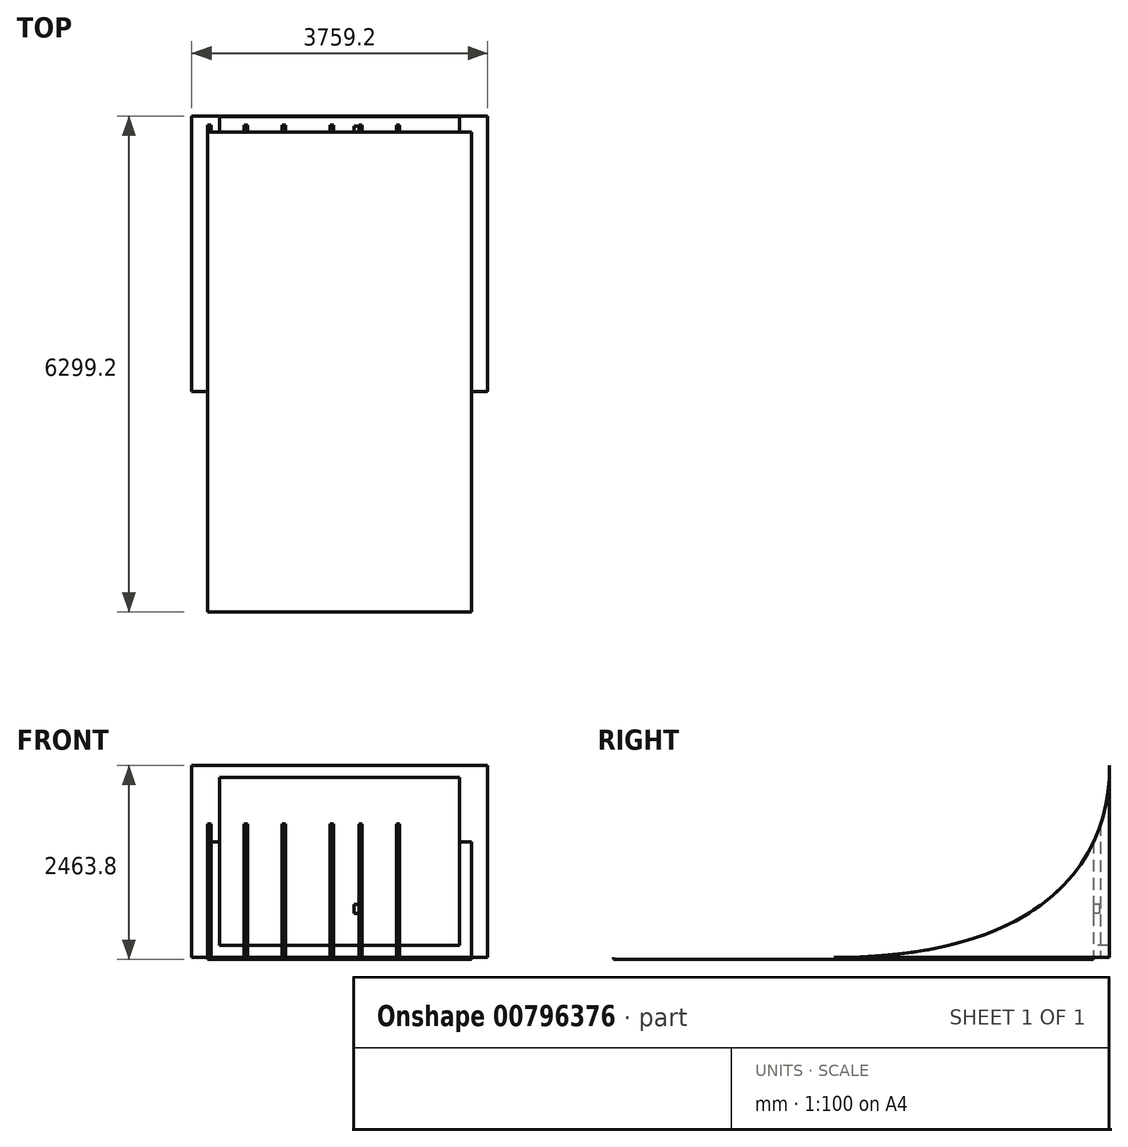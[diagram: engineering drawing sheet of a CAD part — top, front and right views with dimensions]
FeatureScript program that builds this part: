
annotation { "Feature Type Name" : "Feature", "Feature Type Description" : "" }
export const myFeature = defineFeature(function(context is Context, id is Id, definition is map)
    precondition{}
    {
        {
            var Q0;
            Q0=qCreatedBy(makeId("Top.planeOp"),FACE);
            var sketch = newSketch(context, id + "F0", { "sketchPlane" : qUnion([Q0])});
            skLineSegment(sketch, "E0.bottom", {"start": v(-1681.8, 4149.45) * mm, "end": v(1671, 4149.45) * mm});
            skLineSegment(sketch, "E0.top", {"start": v(-1681.8, -1946.55) * mm, "end": v(1671, -1946.55) * mm});
            skLineSegment(sketch, "E0.left", {"start": v(-1681.8, 4149.45) * mm, "end": v(-1681.8, -1946.55) * mm});
            skLineSegment(sketch, "E0.right", {"start": v(1671, 4149.45) * mm, "end": v(1671, -1946.55) * mm});
            skSolve(sketch);
        }
        {
            var Q0;
            Q0=makeQuery(id+"F0.imprint","IMPRINT",FACE,{"disambiguationData":[TD([[makeQuery(id+"F0.imprint","IMPRINT",EDGE,{"derivedFrom":sQuery(id+"F0.wireOp",EDGE,"E0.bottom")}),-1.0]])]});
            extrude(context, id + "F1", {"entities" : qUnion([Q0]), "depth" : 25.4 * mm, "offsetDistance" : 25.4 * mm});
        }
        {
            var Q0;
            Q0=makeQuery(id+"F1.opExtrude","CAP_FACE",FACE,{"disambiguationData":[OSD([sQuery(id+"F0.wireOp",EDGE,"E0.bottom"),sQuery(id+"F0.wireOp",EDGE,"E0.top"),sQuery(id+"F0.wireOp",EDGE,"E0.left"),sQuery(id+"F0.wireOp",EDGE,"E0.right")])],"isStart":false});
            var sketch = newSketch(context, id + "F2", { "sketchPlane" : qUnion([Q0])});
            skLineSegment(sketch, "E1.left", {"start": v(-1681.8, 4149.45) * mm, "end": v(-1681.8, -1946.55) * mm});
            skLineSegment(sketch, "E2.left", {"start": v(1671, 4149.45) * mm, "end": v(1671, -1946.55) * mm});
            skLineSegment(sketch, "E3.0", {"start": v(-1885, 4352.65) * mm, "end": v(-1885, -1946.55) * mm});
            skLineSegment(sketch, "E3.1", {"start": v(-1885, 4352.65) * mm, "end": v(1874.2, 4352.65) * mm});
            skLineSegment(sketch, "E3.2", {"start": v(1874.2, 4352.65) * mm, "end": v(1874.2, -1946.55) * mm});
            skLineSegment(sketch, "E4", {"start": v(-1885, -1946.55) * mm, "end": v(-1681.8, -1946.55) * mm});
            skLineSegment(sketch, "E5", {"start": v(1671, -1946.55) * mm, "end": v(1874.2, -1946.55) * mm});
            skSolve(sketch);
        }
        {
            var Q0;
            Q0=makeQuery(id+"F2.imprint","IMPRINT",FACE,{"disambiguationData":[TD([[makeQuery(id+"F2.imprint","IMPRINT",EDGE,{"derivedFrom":sQuery(id+"F2.wireOp",EDGE,"E1.left")}),-1.0]])]});
            extrude(context, id + "F3", {"entities" : qUnion([Q0]), "depth" : 2438.4 * mm, "offsetDistance" : 25.4 * mm});
        }
        {
            var Q0;
            Q0=makeQuery(id+"F3.opExtrude","SWEPT_FACE",FACE,{"disambiguationData":[OSD([sQuery(id+"F2.wireOp",EDGE,"E3.2")])]});
            var sketch = newSketch(context, id + "F4", { "sketchPlane" : qUnion([Q0])});
            skLineSegment(sketch, "E6", {"start": v(4352.65, 25.4) * mm, "end": v(852.14, 25.4) * mm, "construction": true});
            skFitSpline(sketch, "E7", {"points": [v(4352.65, 2463.8) * mm, v(852.14, 25.4) * mm], "startDerivative": vector(0, -3890.45) * mm, "endDerivative": vector(-7720.83, 0) * mm});
            skSolve(sketch);
        }
        {
            var Q0;
            Q0=makeQuery(id+"F3.opExtrude","SWEPT_FACE",FACE,{"disambiguationData":[OSD([sQuery(id+"F0.wireOp",EDGE,"E0.bottom")])]});
            var sketch = newSketch(context, id + "F5", { "sketchPlane" : qUnion([Q0])});
            skLineSegment(sketch, "E8.0", {"start": v(-1529.4, 2311.4) * mm, "end": v(-1529.4, 177.8) * mm});
            skLineSegment(sketch, "E8.1", {"start": v(-1529.4, 2311.4) * mm, "end": v(1518.6, 2311.4) * mm});
            skLineSegment(sketch, "E8.2", {"start": v(1518.6, 2311.4) * mm, "end": v(1518.6, 177.8) * mm});
            skLineSegment(sketch, "E8.3", {"start": v(-1529.4, 177.8) * mm, "end": v(1518.6, 177.8) * mm});
            skLineSegment(sketch, "E9.0", {"start": v(1664.65, 31.75) * mm, "end": v(1664.65, 2457.45) * mm});
            skLineSegment(sketch, "E9.1", {"start": v(-1675.45, 31.75) * mm, "end": v(1664.65, 31.75) * mm});
            skLineSegment(sketch, "E9.2", {"start": v(-1675.45, 2457.45) * mm, "end": v(-1675.45, 31.75) * mm});
            skLineSegment(sketch, "E9.3", {"start": v(1664.65, 2457.45) * mm, "end": v(-1675.45, 2457.45) * mm});
            skSolve(sketch);
        }
        {
            var Q0;
            Q0=makeQuery(id+"F5.imprint","IMPRINT",FACE,{"disambiguationData":[TD([[makeQuery(id+"F5.imprint","IMPRINT",EDGE,{"derivedFrom":sQuery(id+"F5.wireOp",EDGE,"E8.0")}),1.0]])]});
            extrude(context, id + "F6", {"entities" : qUnion([Q0]), "operationType" : NewBodyOperationType.REMOVE, "endBound" : BoundingType.UP_TO_NEXT, "oppositeDirection" : true, "depth" : 203.2 * mm, "offsetDistance" : 25.4 * mm});
        }
        {
            var Q0;
            Q0=makeQuery(id+"F3.opExtrude","SWEPT_FACE",FACE,{"disambiguationData":[OSD([sQuery(id+"F0.wireOp",EDGE,"E0.bottom")])]});
            var sketch = newSketch(context, id + "F7", { "sketchPlane" : qUnion([Q0])});
            skLineSegment(sketch, "E10.bottom", {"start": v(-1681.8, 2463.8) * mm, "end": v(-1638.62, 2463.8) * mm});
            skLineSegment(sketch, "E10.top", {"start": v(-1681.8, 25.4) * mm, "end": v(-1638.62, 25.4) * mm});
            skLineSegment(sketch, "E10.left", {"start": v(-1681.8, 2463.8) * mm, "end": v(-1681.8, 25.4) * mm});
            skLineSegment(sketch, "E10.right", {"start": v(-1638.62, 2463.8) * mm, "end": v(-1638.62, 25.4) * mm});
            skLineSegment(sketch, "E11.bottom", {"start": v(-1220.8, 2463.8) * mm, "end": v(-1177.61, 2463.8) * mm});
            skLineSegment(sketch, "E11.top", {"start": v(-1220.8, 25.4) * mm, "end": v(-1177.61, 25.4) * mm});
            skLineSegment(sketch, "E11.left", {"start": v(-1220.8, 2463.8) * mm, "end": v(-1220.8, 25.4) * mm});
            skLineSegment(sketch, "E11.right", {"start": v(-1177.61, 2463.8) * mm, "end": v(-1177.61, 25.4) * mm});
            skLineSegment(sketch, "E12", {"start": v(-1199.2, 2463.8) * mm, "end": v(-1681.8, 2463.8) * mm});
            skLineSegment(sketch, "E13.bottom", {"start": v(-738.2, 2463.8) * mm, "end": v(-695.01, 2463.8) * mm});
            skLineSegment(sketch, "E13.top", {"start": v(-738.2, 25.4) * mm, "end": v(-695.01, 25.4) * mm});
            skLineSegment(sketch, "E13.left", {"start": v(-738.2, 2463.8) * mm, "end": v(-738.2, 25.4) * mm});
            skLineSegment(sketch, "E13.right", {"start": v(-695.01, 2463.8) * mm, "end": v(-695.01, 25.4) * mm});
            skLineSegment(sketch, "E14", {"start": v(-1681.8, 2463.8) * mm, "end": v(-716.6, 2463.8) * mm});
            skLineSegment(sketch, "E15.bottom", {"start": v(-128.6, 2463.8) * mm, "end": v(-85.41, 2463.8) * mm});
            skLineSegment(sketch, "E15.top", {"start": v(-128.6, 25.4) * mm, "end": v(-85.41, 25.4) * mm});
            skLineSegment(sketch, "E15.left", {"start": v(-128.6, 2463.8) * mm, "end": v(-128.6, 25.4) * mm});
            skLineSegment(sketch, "E15.right", {"start": v(-85.41, 2463.8) * mm, "end": v(-85.41, 25.4) * mm});
            skLineSegment(sketch, "E16", {"start": v(-107, 2463.8) * mm, "end": v(-1681.8, 2463.8) * mm});
            skLineSegment(sketch, "E17.bottom", {"start": v(237.17, 2463.8) * mm, "end": v(280.35, 2463.8) * mm});
            skLineSegment(sketch, "E17.top", {"start": v(237.17, 25.4) * mm, "end": v(280.35, 25.4) * mm});
            skLineSegment(sketch, "E17.left", {"start": v(237.17, 2463.8) * mm, "end": v(237.17, 25.4) * mm});
            skLineSegment(sketch, "E17.right", {"start": v(280.35, 2463.8) * mm, "end": v(280.35, 25.4) * mm});
            skLineSegment(sketch, "E18", {"start": v(258.76, 2463.8) * mm, "end": v(-1681.8, 2463.8) * mm});
            skLineSegment(sketch, "E19.bottom", {"start": v(712.65, 2463.8) * mm, "end": v(755.83, 2463.8) * mm});
            skLineSegment(sketch, "E19.top", {"start": v(712.65, 25.4) * mm, "end": v(755.83, 25.4) * mm});
            skLineSegment(sketch, "E19.left", {"start": v(712.65, 2463.8) * mm, "end": v(712.65, 25.4) * mm});
            skLineSegment(sketch, "E19.right", {"start": v(755.83, 2463.8) * mm, "end": v(755.83, 25.4) * mm});
            skLineSegment(sketch, "E20", {"start": v(734.24, 2463.8) * mm, "end": v(-1681.8, 2463.8) * mm});
            skSolve(sketch);
        }
        {
            var Q0;
            Q0 = qSketchRegion(id + "F7", true);
            extrude(context, id + "F8", {"entities" : qUnion([Q0]), "oppositeDirection" : true, "depth" : 88.9 * mm, "offsetDistance" : 25.4 * mm});
        }
        {
            var Q0;
            {var subQ0=sQuery(id+"F7.wireOp",EDGE,"E20");Q0=makeQuery(id+"F8.boolean.opBoolean","MERGE",FACE,{"derivedFrom":[makeQuery(id+"F3.opExtrude","SWEPT_FACE",FACE,{"disambiguationData":[OSD([sQuery(id+"F0.wireOp",EDGE,"E0.bottom")])]}),makeQuery(id+"F8.opExtrude","CAP_FACE",FACE,{"disambiguationData":[OSD([sQuery(id+"F7.wireOp",EDGE,"E11.top"),sQuery(id+"F7.wireOp",EDGE,"E11.left"),sQuery(id+"F7.wireOp",EDGE,"E11.right"),subQ0])],"isStart":true}),makeQuery(id+"F8.opExtrude","CAP_FACE",FACE,{"disambiguationData":[OSD([sQuery(id+"F7.wireOp",EDGE,"E13.top"),sQuery(id+"F7.wireOp",EDGE,"E13.left"),sQuery(id+"F7.wireOp",EDGE,"E13.right"),subQ0])],"isStart":true}),makeQuery(id+"F8.opExtrude","CAP_FACE",FACE,{"disambiguationData":[OSD([sQuery(id+"F7.wireOp",EDGE,"E15.top"),sQuery(id+"F7.wireOp",EDGE,"E15.left"),sQuery(id+"F7.wireOp",EDGE,"E15.right"),subQ0])],"isStart":true}),makeQuery(id+"F8.opExtrude","CAP_FACE",FACE,{"disambiguationData":[OSD([sQuery(id+"F7.wireOp",EDGE,"E17.top"),sQuery(id+"F7.wireOp",EDGE,"E17.left"),sQuery(id+"F7.wireOp",EDGE,"E17.right"),subQ0])],"isStart":true}),makeQuery(id+"F8.opExtrude","CAP_FACE",FACE,{"disambiguationData":[OSD([sQuery(id+"F7.wireOp",EDGE,"E19.bottom"),sQuery(id+"F7.wireOp",EDGE,"E19.top"),sQuery(id+"F7.wireOp",EDGE,"E19.left"),sQuery(id+"F7.wireOp",EDGE,"E19.right"),subQ0])],"isStart":true})]});}
            var sketch = newSketch(context, id + "F9", { "sketchPlane" : qUnion([Q0])});
            skLineSegment(sketch, "E21.bottom", {"start": v(237.17, 698.5) * mm, "end": v(173.67, 698.5) * mm});
            skLineSegment(sketch, "E21.top", {"start": v(237.17, 584.2) * mm, "end": v(173.67, 584.2) * mm});
            skLineSegment(sketch, "E21.left", {"start": v(237.17, 698.5) * mm, "end": v(237.17, 584.2) * mm});
            skLineSegment(sketch, "E21.right", {"start": v(173.67, 698.5) * mm, "end": v(173.67, 584.2) * mm});
            skLineSegment(sketch, "E22", {"start": v(237.17, 584.2) * mm, "end": v(237.17, 177.8) * mm, "construction": true});
            skCircle(sketch, "E23", {"center": v(206.47, 669.37) * mm, "radius": 18.27 * mm});
            skLineSegment(sketch, "E24", {"start": v(173.67, 641.35) * mm, "end": v(237.17, 641.35) * mm});
            skCircle(sketch, "E25", {"center": v(206.48, 613.44) * mm, "radius": 18.27 * mm});
            skLineSegment(sketch, "E26", {"start": v(200.19, 622.8) * mm, "end": v(200.19, 611.5) * mm});
            skLineSegment(sketch, "E27", {"start": v(213.83, 623.18) * mm, "end": v(213.83, 611.51) * mm});
            skLineSegment(sketch, "E28", {"start": v(199.6, 680.33) * mm, "end": v(199.6, 670.38) * mm});
            skLineSegment(sketch, "E29", {"start": v(214.24, 680.67) * mm, "end": v(214.24, 669.67) * mm});
            skLineSegment(sketch, "E30", {"start": v(209.05, 604.4) * mm, "end": v(206.48, 604.4) * mm});
            skLineSegment(sketch, "E31", {"start": v(209.3, 662.39) * mm, "end": v(206.48, 662.39) * mm});
            skSolve(sketch);
        }
        {
            var Q0;
            {var subQ2=sQuery(id+"F9.wireOp",EDGE,"E21.top");Q0=makeQuery(id+"F9.imprint","IMPRINT",FACE,{"disambiguationData":[TD([[makeQuery(id+"F9.imprint","IMPRINT",EDGE,{"derivedFrom":subQ2}),-1.0]])]});}
            var Q1;
            Q1=makeQuery(id+"F9.imprint","IMPRINT",FACE,{"disambiguationData":[TD([[makeQuery(id+"F9.imprint","IMPRINT",EDGE,{"derivedFrom":sQuery(id+"F9.wireOp",EDGE,"E25")}),1.0]])]});
            var Q2;
            {var subQ1=sQuery(id+"F9.wireOp",EDGE,"E21.bottom");Q2=makeQuery(id+"F9.imprint","IMPRINT",FACE,{"disambiguationData":[TD([[makeQuery(id+"F9.imprint","IMPRINT",EDGE,{"derivedFrom":subQ1}),1.0]])]});}
            var Q3;
            Q3=makeQuery(id+"F9.imprint","IMPRINT",FACE,{"disambiguationData":[TD([[makeQuery(id+"F9.imprint","IMPRINT",EDGE,{"derivedFrom":sQuery(id+"F9.wireOp",EDGE,"E23")}),1.0]])]});
            extrude(context, id + "F10", {"entities" : qUnion([Q0, Q1, Q2, Q3]), "oppositeDirection" : true, "depth" : 76.2 * mm, "offsetDistance" : 25.4 * mm});
        }
        {
            var Q0;
            {var subQ0=sQuery(id+"F4.wireOp",EDGE,"E7");Q0=makeQuery(id+"F4.imprint","IMPRINT",FACE,{"disambiguationData":[TD([[makeQuery(id+"F4.imprint","IMPRINT",EDGE,{"derivedFrom":subQ0}),-1.0]])]});}
            extrude(context, id + "F11", {"entities" : qUnion([Q0]), "operationType" : NewBodyOperationType.REMOVE, "endBound" : BoundingType.THROUGH_ALL, "oppositeDirection" : true, "depth" : 25.4 * mm, "offsetDistance" : 25.4 * mm});
        }
    });
